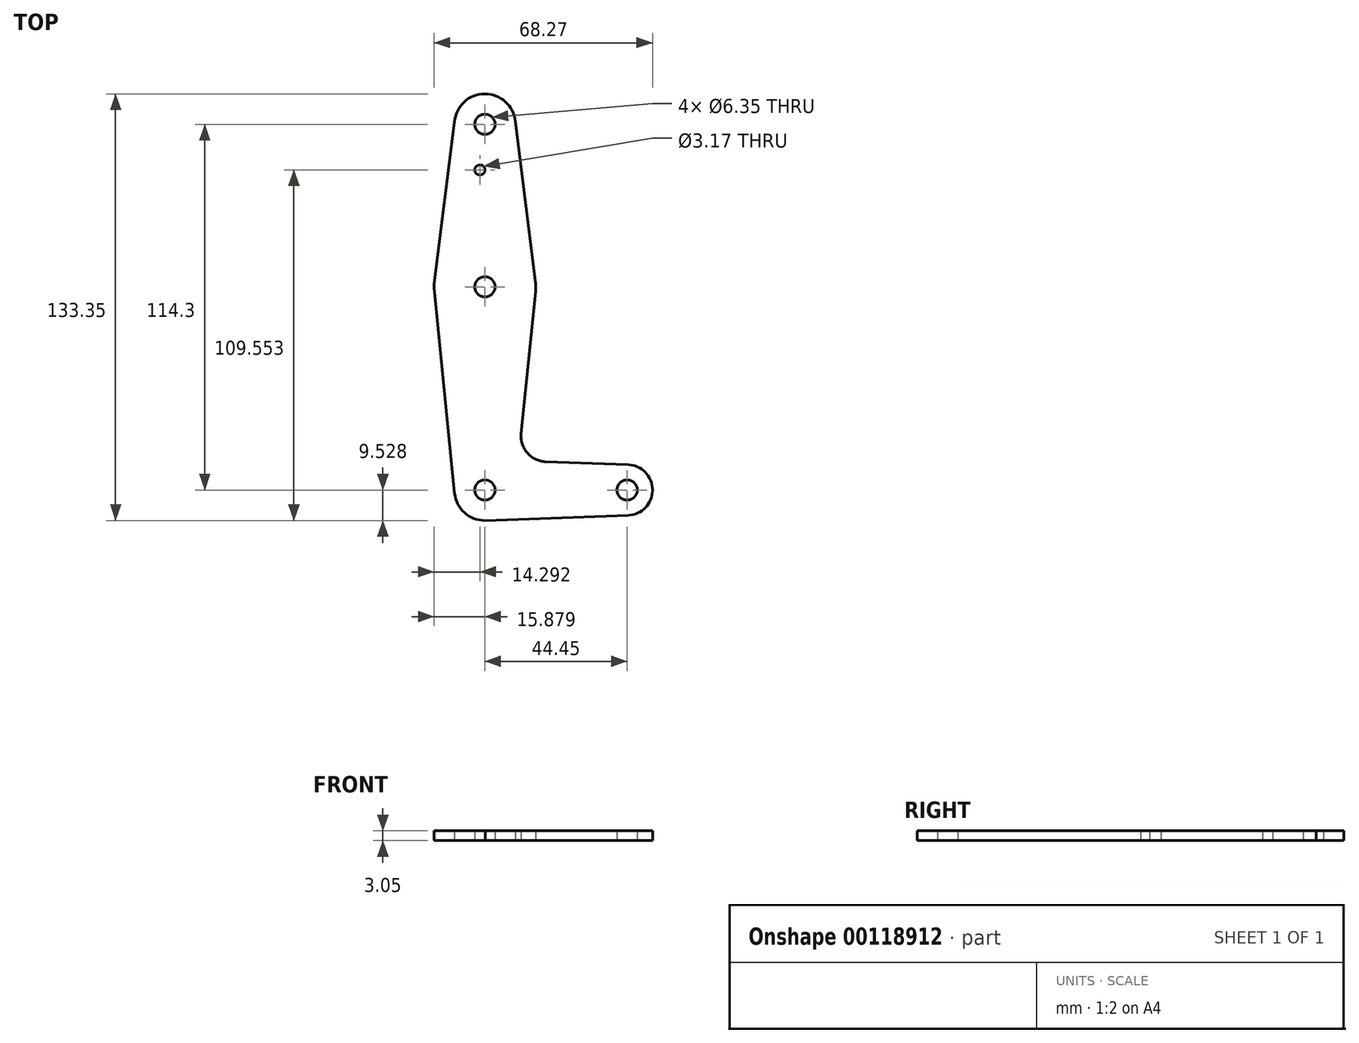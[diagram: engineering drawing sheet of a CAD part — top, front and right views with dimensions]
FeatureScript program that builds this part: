
annotation { "Feature Type Name" : "Feature", "Feature Type Description" : "" }
export const myFeature = defineFeature(function(context is Context, id is Id, definition is map)
    precondition{}
    {
        {
            var Q0;
            Q0=qCreatedBy(makeId("Top.planeOp"),FACE);
            var sketch = newSketch(context, id + "F0", { "sketchPlane" : qUnion([Q0])});
            skLineSegment(sketch, "E0", {"start": v(-32.34, 64.22) * mm, "end": v(-32.34, -50.08) * mm});
            skLineSegment(sketch, "E1", {"start": v(-32.34, -50.08) * mm, "end": v(12.1, -50.08) * mm});
            skCircle(sketch, "E2", {"center": v(-32.34, 64.22) * mm, "radius": 9.53 * mm});
            skCircle(sketch, "E3", {"center": v(-32.34, 13.42) * mm, "radius": 15.88 * mm});
            skCircle(sketch, "E4", {"center": v(-32.34, -50.08) * mm, "radius": 9.53 * mm});
            skCircle(sketch, "E5", {"center": v(12.1, -50.08) * mm, "radius": 7.94 * mm});
            skLineSegment(sketch, "E6", {"start": v(-16.53, 11.98) * mm, "end": v(-21, -32.5) * mm});
            skLineSegment(sketch, "E7", {"start": v(-48.21, 13.08) * mm, "end": v(-41.82, -51.03) * mm});
            skLineSegment(sketch, "E8", {"start": v(-32.2, -59.6) * mm, "end": v(12.4, -58.01) * mm});
            skLineSegment(sketch, "E9", {"start": v(-13.37, -41.23) * mm, "end": v(12.4, -42.15) * mm});
            skArc(sketch, "E10.filletArc", {"start": v(-21, -32.5) * mm, "mid": v(-19.08, -38.51) * mm, "end": v(-13.37, -41.23) * mm});
            skCircle(sketch, "E11", {"center": v(-32.34, -50.08) * mm, "radius": 3.18 * mm});
            skCircle(sketch, "E12", {"center": v(12.1, -50.08) * mm, "radius": 3.18 * mm});
            skCircle(sketch, "E13", {"center": v(-32.34, 64.22) * mm, "radius": 3.18 * mm});
            skCircle(sketch, "E14", {"center": v(-33.93, 49.94) * mm, "radius": 1.59 * mm});
            skCircle(sketch, "E15", {"center": v(-32.34, 13.42) * mm, "radius": 3.18 * mm});
            skLineSegment(sketch, "E16", {"start": v(-22.86, 65.11) * mm, "end": v(-16.53, 14.93) * mm});
            skLineSegment(sketch, "E17", {"start": v(-41.84, 64.9) * mm, "end": v(-48.1, 15.4) * mm});
            skSolve(sketch);
        }
        {
            var Q0;
            {var subQ0=sQuery(id+"F0.wireOp",EDGE,"Em6Xr3xS-y4QU-jXdP-CDwQ-ucvUUCw51Xsq");Q0=makeQuery(id+"F0.imprint","IMPRINT",FACE,{"disambiguationData":[TD([[makeQuery(id+"F0.imprint","IMPRINT",EDGE,{"derivedFrom":subQ0}),1.0]])]});}
            var Q1;
            {var subQ0=sQuery(id+"F0.wireOp",EDGE,"E5");var subQ1=sQuery(id+"F0.wireOp",EDGE,"E1");var subQ2=makeQuery(id+"F0.imprint","INTERSECT",VERTEX,{"derivedFrom":[subQ1,subQ0]});Q1=makeQuery(id+"F0.imprint","IMPRINT",FACE,{"disambiguationData":[TD([[makeQuery(id+"F0.imprint","IMPRINT",EDGE,{"disambiguationData":[TD([[subQ2,1.0]])],"derivedFrom":subQ1}),-1.0]])]});}
            var Q2;
            {var subQ0=sQuery(id+"F0.wireOp",EDGE,"E4");var subQ2=sQuery(id+"F0.wireOp",EDGE,"E0");var subQ3=makeQuery(id+"F0.imprint","INTERSECT",VERTEX,{"derivedFrom":[subQ2,subQ0]});Q2=makeQuery(id+"F0.imprint","IMPRINT",FACE,{"disambiguationData":[TD([[makeQuery(id+"F0.imprint","IMPRINT",EDGE,{"disambiguationData":[TD([[subQ3,-1.0]])],"derivedFrom":subQ2}),-1.0]])]});}
            var Q3;
            {var subQ0=sQuery(id+"F0.wireOp",EDGE,"E4");var subQ1=sQuery(id+"F0.wireOp",EDGE,"E0");var subQ2=makeQuery(id+"F0.imprint","INTERSECT",VERTEX,{"derivedFrom":[subQ1,subQ0]});Q3=makeQuery(id+"F0.imprint","IMPRINT",FACE,{"disambiguationData":[TD([[makeQuery(id+"F0.imprint","IMPRINT",EDGE,{"disambiguationData":[TD([[subQ2,-1.0]])],"derivedFrom":subQ1}),1.0]])]});}
            var Q4;
            Q4=makeQuery(id+"F0.imprint","IMPRINT",FACE,{"disambiguationData":[TD([[makeQuery(id+"F0.imprint","IMPRINT",EDGE,{"derivedFrom":sQuery(id+"F0.wireOp",EDGE,"E12")}),-1.0]])]});
            var Q5;
            {var subQ0=sQuery(id+"F0.wireOp",EDGE,"E3");var subQ2=sQuery(id+"F0.wireOp",EDGE,"E0");var subQ3=makeQuery(id+"F0.imprint","INTERSECT",VERTEX,{"disambiguationData":[OD(0.0)],"derivedFrom":[subQ2,subQ0]});Q5=makeQuery(id+"F0.imprint","IMPRINT",FACE,{"disambiguationData":[TD([[makeQuery(id+"F0.imprint","IMPRINT",EDGE,{"disambiguationData":[TD([[subQ3,-1.0]])],"derivedFrom":subQ2}),-1.0]])]});}
            var Q6;
            {var subQ0=sQuery(id+"F0.wireOp",EDGE,"FHDHuRb0-ALtu-ZHOv-vF7F-7ldGrWvC21tF");Q6=makeQuery(id+"F0.imprint","IMPRINT",FACE,{"disambiguationData":[TD([[makeQuery(id+"F0.imprint","IMPRINT",EDGE,{"derivedFrom":subQ0}),-1.0]])]});}
            var Q7;
            {var subQ0=sQuery(id+"F0.wireOp",EDGE,"E3");var subQ2=sQuery(id+"F0.wireOp",EDGE,"E0");var subQ3=makeQuery(id+"F0.imprint","INTERSECT",VERTEX,{"disambiguationData":[OD(0.0)],"derivedFrom":[subQ2,subQ0]});Q7=makeQuery(id+"F0.imprint","IMPRINT",FACE,{"disambiguationData":[TD([[makeQuery(id+"F0.imprint","IMPRINT",EDGE,{"disambiguationData":[TD([[subQ3,-1.0]])],"derivedFrom":subQ2}),1.0]])]});}
            var Q8;
            {var subQ0=sQuery(id+"F0.wireOp",EDGE,"E3");var subQ1=sQuery(id+"F0.wireOp",EDGE,"E0");var subQ2=makeQuery(id+"F0.imprint","INTERSECT",VERTEX,{"disambiguationData":[OD(1.0)],"derivedFrom":[subQ1,subQ0]});Q8=makeQuery(id+"F0.imprint","IMPRINT",FACE,{"disambiguationData":[TD([[makeQuery(id+"F0.imprint","IMPRINT",EDGE,{"disambiguationData":[TD([[subQ2,-1.0]])],"derivedFrom":subQ1}),-1.0]])]});}
            var Q9;
            Q9=makeQuery(id+"F0.imprint","IMPRINT",FACE,{"disambiguationData":[TD([[makeQuery(id+"F0.imprint","IMPRINT",EDGE,{"derivedFrom":sQuery(id+"F0.wireOp",EDGE,"E13")}),-1.0]])]});
            var Q10;
            {var subQ12=sQuery(id+"F0.wireOp",EDGE,"E9");Q10=makeQuery(id+"F0.imprint","IMPRINT",FACE,{"disambiguationData":[TD([[makeQuery(id+"F0.imprint","IMPRINT",EDGE,{"derivedFrom":subQ12}),-1.0]])]});}
            var Q11;
            {var subQ0=sQuery(id+"F0.wireOp",EDGE,"E7");var subQ1=sQuery(id+"F0.wireOp",EDGE,"E3");var subQ2=makeQuery(id+"F0.imprint","INTERSECT",VERTEX,{"disambiguationData":[OD(0.0)],"derivedFrom":[subQ1,subQ0]});Q11=makeQuery(id+"F0.imprint","IMPRINT",FACE,{"disambiguationData":[TD([[makeQuery(id+"F0.imprint","IMPRINT",EDGE,{"disambiguationData":[TD([[subQ2,-1.0]])],"derivedFrom":subQ1}),1.0]])]});}
            var Q12;
            {var subQ0=sQuery(id+"F0.wireOp",EDGE,"E8");var subQ1=sQuery(id+"F0.wireOp",EDGE,"E4");var subQ2=makeQuery(id+"F0.imprint","INTERSECT",VERTEX,{"disambiguationData":[OD(0.0)],"derivedFrom":[subQ1,subQ0]});Q12=makeQuery(id+"F0.imprint","IMPRINT",FACE,{"disambiguationData":[TD([[makeQuery(id+"F0.imprint","IMPRINT",EDGE,{"disambiguationData":[TD([[subQ2,-1.0]])],"derivedFrom":subQ1}),1.0]])]});}
            var Q13;
            {var subQ0=sQuery(id+"F0.wireOp",EDGE,"E6");var subQ1=sQuery(id+"F0.wireOp",EDGE,"E3");var subQ2=makeQuery(id+"F0.imprint","INTERSECT",VERTEX,{"disambiguationData":[OD(0.0)],"derivedFrom":[subQ1,subQ0]});Q13=makeQuery(id+"F0.imprint","IMPRINT",FACE,{"disambiguationData":[TD([[makeQuery(id+"F0.imprint","IMPRINT",EDGE,{"disambiguationData":[TD([[subQ2,1.0]])],"derivedFrom":subQ1}),1.0]])]});}
            var Q14;
            {var subQ6=sQuery(id+"F0.wireOp",EDGE,"E14");Q14=makeQuery(id+"F0.imprint","IMPRINT",FACE,{"disambiguationData":[TD([[makeQuery(id+"F0.imprint","IMPRINT",EDGE,{"derivedFrom":subQ6}),-1.0]])]});}
            var Q15;
            {var subQ0=sQuery(id+"F0.wireOp",EDGE,"sWZ03T7J-mkHB-LJ8R-dhFq-Zf7rXJBKRYwX");Q15=makeQuery(id+"F0.imprint","IMPRINT",FACE,{"disambiguationData":[TD([[makeQuery(id+"F0.imprint","IMPRINT",EDGE,{"derivedFrom":subQ0}),-1.0]])]});}
            var Q16;
            {var subQ3=sQuery(id+"F0.wireOp",EDGE,"E0");var subQ8=makeQuery(id+"F0.imprint","INTERSECT",VERTEX,{"derivedFrom":[subQ3,sQuery(id+"F0.wireOp",EDGE,"E14")]});Q16=makeQuery(id+"F0.imprint","IMPRINT",FACE,{"disambiguationData":[TD([[makeQuery(id+"F0.imprint","IMPRINT",EDGE,{"disambiguationData":[TD([[subQ8,1.0]])],"derivedFrom":subQ3}),1.0]])]});}
            extrude(context, id + "F1", {"entities" : qUnion([Q0, Q1, Q2, Q3, Q4, Q5, Q6, Q7, Q8, Q9, Q10, Q11, Q12, Q13, Q14, Q15, Q16]), "depth" : 3.05 * mm});
        }
    });
